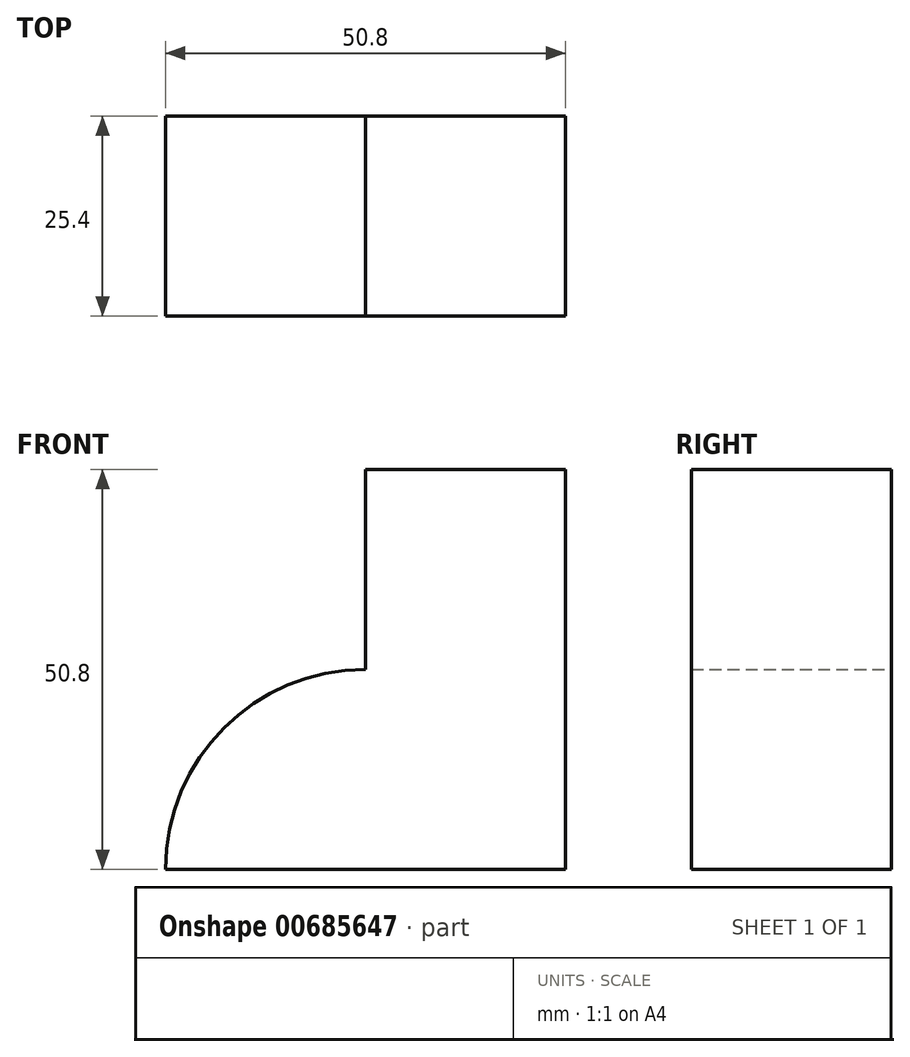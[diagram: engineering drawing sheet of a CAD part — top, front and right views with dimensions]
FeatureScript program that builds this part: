
annotation { "Feature Type Name" : "Feature", "Feature Type Description" : "" }
export const myFeature = defineFeature(function(context is Context, id is Id, definition is map)
    precondition{}
    {
        {
            var Q0;
            Q0=qCreatedBy(makeId("Front.planeOp"),FACE);
            var sketch = newSketch(context, id + "F0", { "sketchPlane" : qUnion([Q0])});
            skLineSegment(sketch, "E0", {"start": v(0, 0) * mm, "end": v(-50.8, 0) * mm});
            skLineSegment(sketch, "E1", {"start": v(0, 0) * mm, "end": v(0, 50.8) * mm});
            skLineSegment(sketch, "E2", {"start": v(0, 50.8) * mm, "end": v(-25.4, 50.8) * mm});
            skLineSegment(sketch, "E3", {"start": v(-25.4, 50.8) * mm, "end": v(-25.4, 25.4) * mm});
            skArc(sketch, "E4", {"start": v(-25.4, 25.4) * mm, "mid": v(-43.36, 17.96) * mm, "end": v(-50.8, 0) * mm});
            skSolve(sketch);
        }
        {
            var Q0;
            Q0 = qSketchRegion(id + "F0", true);
            extrude(context, id + "F1", {"entities" : qUnion([Q0]), "depth" : 25.4 * mm, "offsetDistance" : 25.4 * mm});
        }
    });
